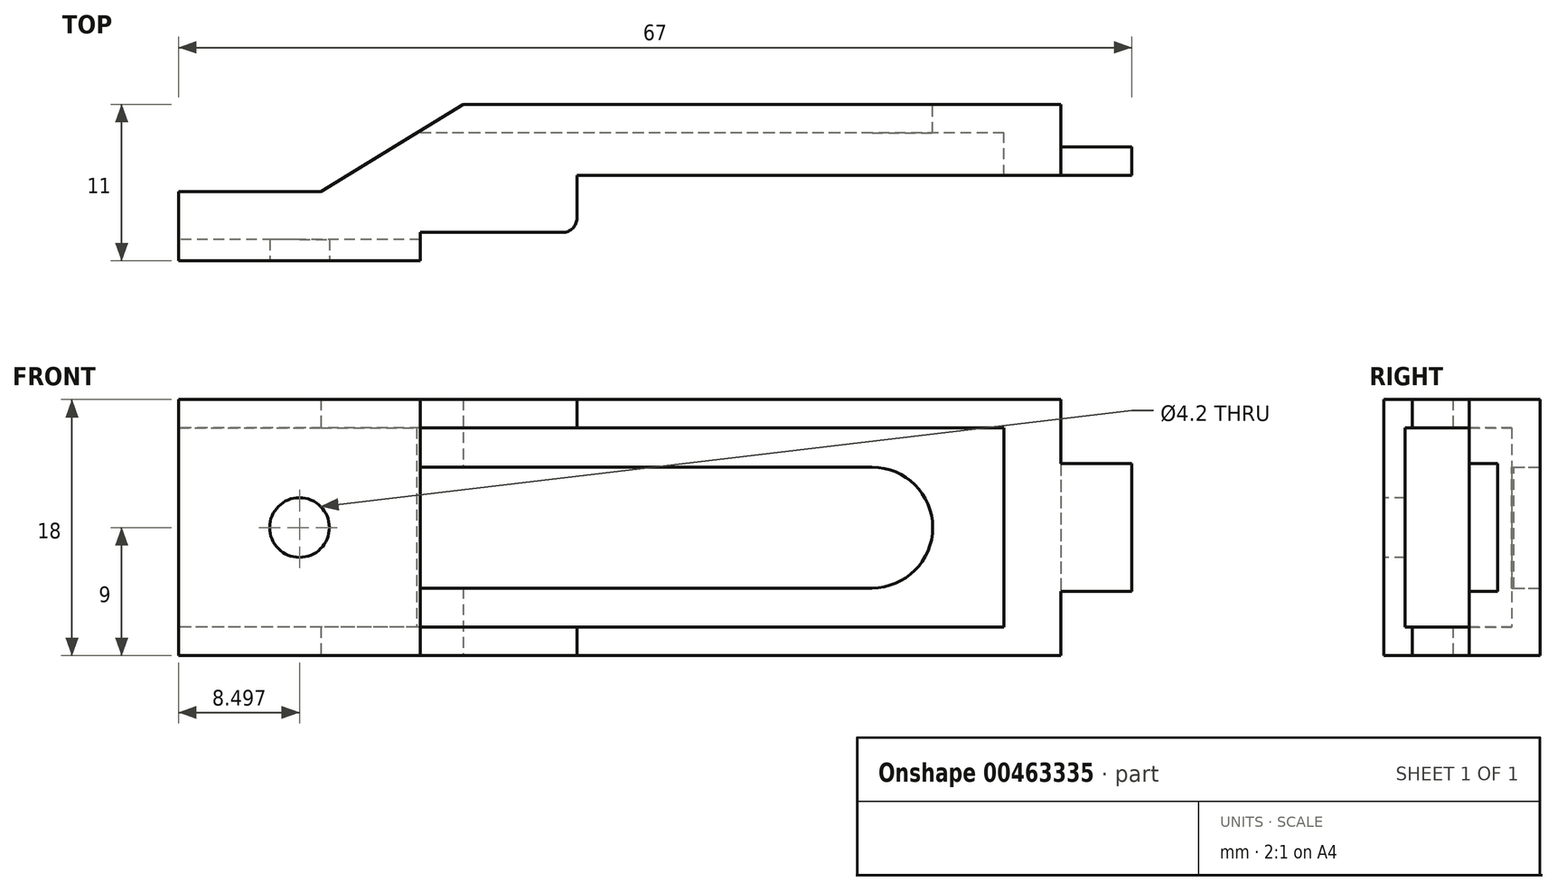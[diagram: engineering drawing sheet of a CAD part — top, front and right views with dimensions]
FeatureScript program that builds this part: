
annotation { "Feature Type Name" : "Feature", "Feature Type Description" : "" }
export const myFeature = defineFeature(function(context is Context, id is Id, definition is map)
    precondition{}
    {
        {
            var Q0;
            Q0=qCreatedBy(makeId("Top.planeOp"),FACE);
            var sketch = newSketch(context, id + "F0", { "sketchPlane" : qUnion([Q0])});
            skLineSegment(sketch, "E0", {"start": v(-49.63, 5.37) * mm, "end": v(-32.63, 5.37) * mm});
            skLineSegment(sketch, "E1", {"start": v(-32.63, 5.37) * mm, "end": v(-32.63, 7.37) * mm});
            skLineSegment(sketch, "E2", {"start": v(-32.63, 7.37) * mm, "end": v(-21.63, 7.37) * mm});
            skLineSegment(sketch, "E3", {"start": v(-21.63, 7.37) * mm, "end": v(-21.63, 11.37) * mm});
            skLineSegment(sketch, "E4", {"start": v(-21.63, 11.37) * mm, "end": v(12.37, 11.37) * mm});
            skLineSegment(sketch, "E5", {"start": v(12.37, 11.37) * mm, "end": v(12.37, 16.37) * mm});
            skLineSegment(sketch, "E6", {"start": v(12.37, 16.37) * mm, "end": v(-29.63, 16.37) * mm});
            skLineSegment(sketch, "E7", {"start": v(-29.63, 16.37) * mm, "end": v(-39.63, 10.23) * mm});
            skLineSegment(sketch, "E8", {"start": v(-39.63, 10.23) * mm, "end": v(-49.63, 10.23) * mm});
            skLineSegment(sketch, "E9", {"start": v(-49.63, 10.23) * mm, "end": v(-49.63, 5.37) * mm});
            skLineSegment(sketch, "E10", {"start": v(12.37, 11.37) * mm, "end": v(17.37, 11.37) * mm});
            skLineSegment(sketch, "E11", {"start": v(17.37, 11.37) * mm, "end": v(17.37, 13.37) * mm});
            skLineSegment(sketch, "E12", {"start": v(17.37, 13.37) * mm, "end": v(12.37, 13.37) * mm});
            skLineSegment(sketch, "E13", {"start": v(12.37, 13.37) * mm, "end": v(12.37, 11.37) * mm});
            skSolve(sketch);
        }
        {
            var Q0;
            Q0=makeQuery(id+"F0.imprint","IMPRINT",FACE,{"disambiguationData":[TD([[makeQuery(id+"F0.imprint","IMPRINT",EDGE,{"derivedFrom":sQuery(id+"F0.wireOp",EDGE,"E0")}),1.0]])]});
            extrude(context, id + "F1", {"entities" : qUnion([Q0]), "endBound" : BoundingType.SYMMETRIC, "depth" : 18 * mm});
        }
        {
            var Q0;
            Q0=makeQuery(id+"F0.imprint","IMPRINT",FACE,{"disambiguationData":[TD([[makeQuery(id+"F0.imprint","IMPRINT",EDGE,{"derivedFrom":sQuery(id+"F0.wireOp",EDGE,"E10")}),1.0]])]});
            extrude(context, id + "F2", {"entities" : qUnion([Q0]), "operationType" : NewBodyOperationType.ADD, "endBound" : BoundingType.SYMMETRIC, "depth" : 9 * mm});
        }
        {
            var Q0;
            Q0=makeQuery(id+"F1.opExtrude","SWEPT_FACE",FACE,{"disambiguationData":[OSD([sQuery(id+"F0.wireOp",EDGE,"E0")])]});
            var sketch = newSketch(context, id + "F3", { "sketchPlane" : qUnion([Q0])});
            skCircle(sketch, "E14", {"center": v(-41.13, 0) * mm, "radius": 2.1 * mm});
            skSolve(sketch);
        }
        {
            var Q0;
            Q0=makeQuery(id+"F3.imprint","IMPRINT",FACE,{"disambiguationData":[TD([[makeQuery(id+"F3.imprint","IMPRINT",EDGE,{"derivedFrom":sQuery(id+"F3.wireOp",EDGE,"E14")}),1.0]])]});
            extrude(context, id + "F4", {"entities" : qUnion([Q0]), "operationType" : NewBodyOperationType.REMOVE, "endBound" : BoundingType.THROUGH_ALL, "oppositeDirection" : true, "depth" : 25 * mm});
        }
        {
            var Q0;
            Q0=makeQuery(id+"F1.opExtrude","SWEPT_FACE",FACE,{"disambiguationData":[OSD([sQuery(id+"F0.wireOp",EDGE,"E6")])]});
            var sketch = newSketch(context, id + "F5", { "sketchPlane" : qUnion([Q0])});
            skLineSegment(sketch, "E15", {"start": v(0.88, -4.25) * mm, "end": v(29.53, -4.25) * mm});
            skLineSegment(sketch, "E16.MirrorCS", {"start": v(0.88, 4.25) * mm, "end": v(29.53, 4.25) * mm});
            skArc(sketch, "E17", {"start": v(0.88, 4.25) * mm, "mid": v(-3.37, 0) * mm, "end": v(0.88, -4.25) * mm});
            skLineSegment(sketch, "E18", {"start": v(29.53, -4.25) * mm, "end": v(32.63, -4.25) * mm});
            skLineSegment(sketch, "E19", {"start": v(29.53, 4.25) * mm, "end": v(32.64, 4.25) * mm});
            skLineSegment(sketch, "E20", {"start": v(32.64, 4.25) * mm, "end": v(32.63, -4.25) * mm});
            skSolve(sketch);
        }
        {
            var Q0;
            {var subQ1=sQuery(id+"F5.wireOp",EDGE,"E15");Q0=makeQuery(id+"F5.imprint","IMPRINT",FACE,{"disambiguationData":[TD([[makeQuery(id+"F5.imprint","IMPRINT",EDGE,{"derivedFrom":subQ1}),1.0]])]});}
            var Q1;
            {var subQ0=sQuery(id+"F5.wireOp",EDGE,"E20");Q1=makeQuery(id+"F5.imprint","IMPRINT",FACE,{"disambiguationData":[TD([[makeQuery(id+"F5.imprint","IMPRINT",EDGE,{"derivedFrom":subQ0}),-1.0]])]});}
            extrude(context, id + "F6", {"entities" : qUnion([Q0, Q1]), "operationType" : NewBodyOperationType.REMOVE, "endBound" : BoundingType.THROUGH_ALL, "oppositeDirection" : true, "depth" : 25 * mm});
        }
        {
            var Q0;
            Q0=makeQuery(id+"F1.opExtrude","SWEPT_FACE",FACE,{"disambiguationData":[OSD([sQuery(id+"F0.wireOp",EDGE,"E9")])]});
            var sketch = newSketch(context, id + "F7", { "sketchPlane" : qUnion([Q0])});
            skLineSegment(sketch, "E21", {"start": v(-6.87, -7) * mm, "end": v(-14.37, -7) * mm});
            skLineSegment(sketch, "E22", {"start": v(-14.37, -7) * mm, "end": v(-14.37, 7) * mm});
            skLineSegment(sketch, "E23", {"start": v(-14.37, 7) * mm, "end": v(-6.87, 7) * mm});
            skLineSegment(sketch, "E24", {"start": v(-6.87, 7) * mm, "end": v(-6.87, -7) * mm});
            skSolve(sketch);
        }
        {
            var Q0;
            {var subQ0=sQuery(id+"F7.wireOp",EDGE,"E22");Q0=makeQuery(id+"F7.imprint","IMPRINT",FACE,{"disambiguationData":[TD([[makeQuery(id+"F7.imprint","IMPRINT",EDGE,{"derivedFrom":subQ0}),-1.0]])]});}
            var Q1;
            {var subQ0=sQuery(id+"F7.wireOp",EDGE,"E24");Q1=makeQuery(id+"F7.imprint","IMPRINT",FACE,{"disambiguationData":[TD([[makeQuery(id+"F7.imprint","IMPRINT",EDGE,{"derivedFrom":subQ0}),-1.0]])]});}
            extrude(context, id + "F8", {"entities" : qUnion([Q0, Q1]), "operationType" : NewBodyOperationType.REMOVE, "oppositeDirection" : true, "depth" : 58 * mm});
        }
        {
            var Q0;
            {var subQ0=sQuery(id+"F0.wireOp",EDGE,"E3");var subQ1=sQuery(id+"F0.wireOp",EDGE,"E2");Q0=makeQuery(id+"F6.boolean.opBoolean","SPLIT",EDGE,{"disambiguationData":[TD([makeQuery(id+"F6.opExtrude","SWEPT_FACE",FACE,{"disambiguationData":[OSD([sQuery(id+"F5.wireOp",EDGE,"E15"),sQuery(id+"F5.wireOp",EDGE,"E18")])]})])],"derivedFrom":makeQuery(id+"F1.opExtrude","SWEPT_EDGE",EDGE,{"disambiguationData":[OSD([subQ1,subQ0])]})});}
            var Q1;
            {var subQ0=sQuery(id+"F0.wireOp",EDGE,"E3");var subQ1=sQuery(id+"F0.wireOp",EDGE,"E2");Q1=makeQuery(id+"F6.boolean.opBoolean","SPLIT",EDGE,{"disambiguationData":[TD([makeQuery(id+"F6.opExtrude","SWEPT_FACE",FACE,{"disambiguationData":[OSD([sQuery(id+"F5.wireOp",EDGE,"E16.MirrorCS"),sQuery(id+"F5.wireOp",EDGE,"E19")])]})])],"derivedFrom":makeQuery(id+"F1.opExtrude","SWEPT_EDGE",EDGE,{"disambiguationData":[OSD([subQ1,subQ0])]})});}
            fillet(context, id + "F9", {"entities" : qUnion([Q0, Q1]), "radius" : 1 * mm, "tangentPropagation" : true, "allowEdgeOverflow" : false});
        }
    });
